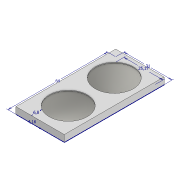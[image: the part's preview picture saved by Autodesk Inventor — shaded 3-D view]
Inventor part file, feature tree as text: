
AUTODESK INVENTOR PART (.ipt)
format: ipt  version: 2020.3 (Build 243373000, 373)  size: 110,592 bytes
history: native  units: mm
features: extrude x3, sketch x2
ambient origin geometry x8: Origin, YZ Plane, XZ Plane, XY Plane, X Axis, Y Axis, Z Axis, Center Point
bodies: Solid1 (feature_tree)
feature tree (5):
  sketch  "Sketch1"  dims[d0=31.0mm d1=64.0mm]
  extrude  "Extrusion1"  Depth=64.0mm
  extrude  "Extrusion2"  Depth=0.5mm
  extrude  "Extrusion3"  Depth=0.5mm
  sketch  "Sketch2"  dims[d2=25.17mm d4=4.16mm d5=6.8mm d6=4.3mm d7=0.0mm d8=1.75mm d9=0.0mm d10=24.5mm d11=4.18mm d13=29.5mm d14=0.5mm d15=0.0mm]
